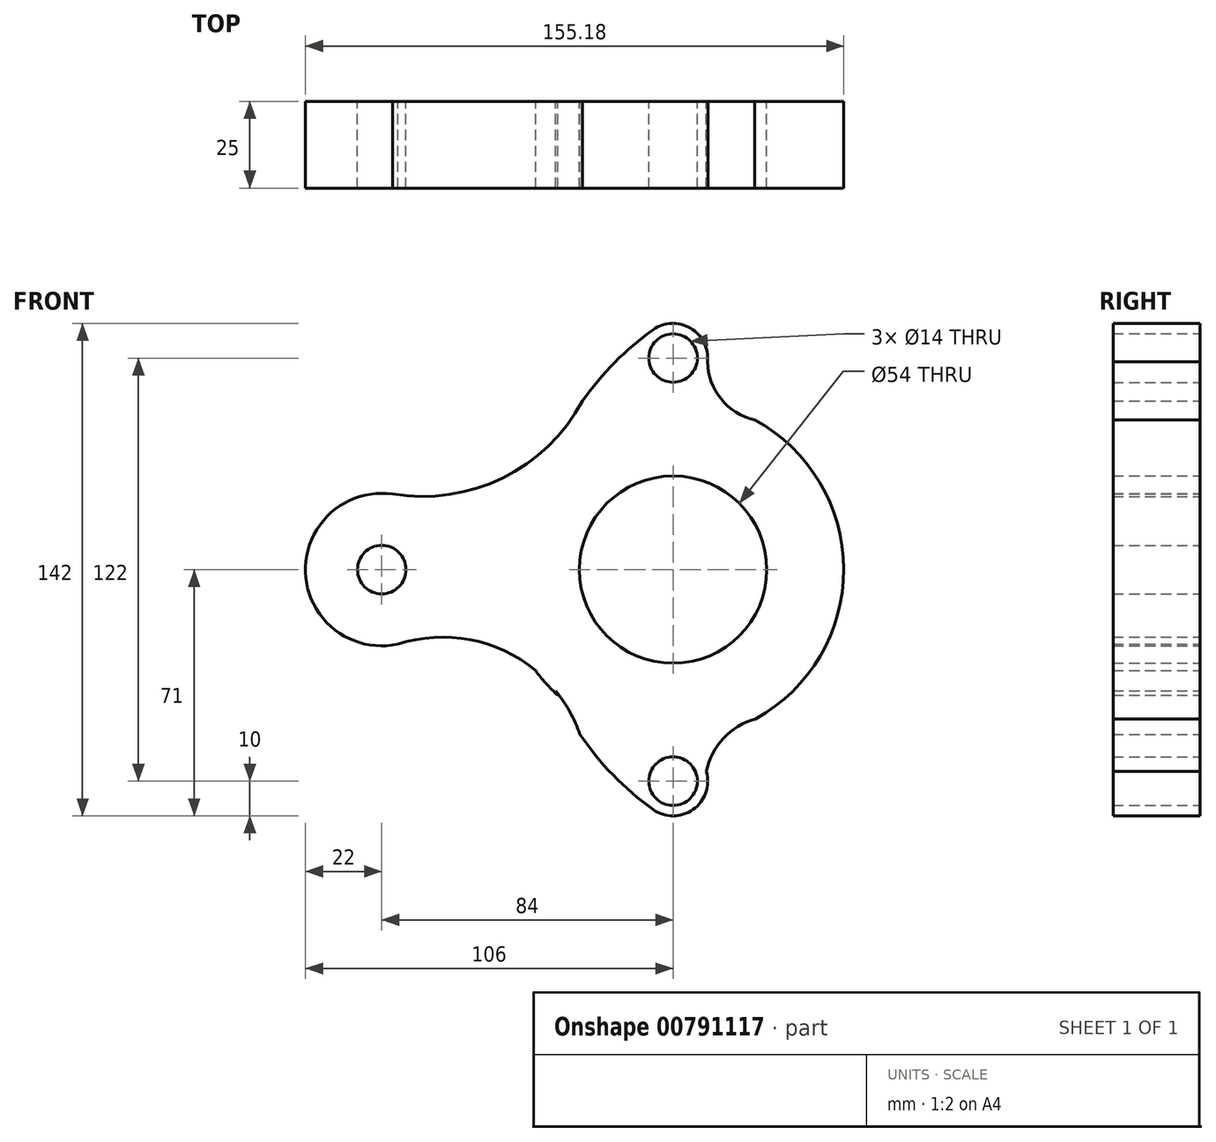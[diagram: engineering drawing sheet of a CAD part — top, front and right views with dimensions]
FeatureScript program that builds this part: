
annotation { "Feature Type Name" : "Feature", "Feature Type Description" : "" }
export const myFeature = defineFeature(function(context is Context, id is Id, definition is map)
    precondition{}
    {
        {
            var Q0;
            Q0=qCreatedBy(makeId("Front.planeOp"),FACE);
            var sketch = newSketch(context, id + "F0", { "sketchPlane" : qUnion([Q0])});
            skArc(sketch, "E0", {"start": v(23.8, -43.04) * mm, "mid": v(49.04, 3.7) * mm, "end": v(17.08, 46.12) * mm});
            skCircle(sketch, "E1", {"center": v(0, 0) * mm, "radius": 27 * mm});
            skLineSegment(sketch, "E2", {"start": v(0, 0) * mm, "end": v(-84, 0) * mm});
            skLineSegment(sketch, "E3", {"start": v(0, 0) * mm, "end": v(0, 61) * mm});
            skLineSegment(sketch, "E4", {"start": v(0, 0) * mm, "end": v(0, -61) * mm});
            skCircle(sketch, "E5", {"center": v(0, 61) * mm, "radius": 7 * mm});
            skCircle(sketch, "E6", {"center": v(0, 61) * mm, "radius": 10 * mm});
            skCircle(sketch, "E7", {"center": v(0, -61) * mm, "radius": 7 * mm});
            skCircle(sketch, "E8", {"center": v(0, -61) * mm, "radius": 10 * mm});
            skCircle(sketch, "E9", {"center": v(-84, 0) * mm, "radius": 7 * mm});
            skArc(sketch, "E10", {"start": v(-80.23, 21.67) * mm, "mid": v(-105.92, -1.9) * mm, "end": v(-76.54, -20.7) * mm});
            skArc(sketch, "E11", {"start": v(-5.82, 69.13) * mm, "mid": v(-16.84, 59.73) * mm, "end": v(-26.1, 48.6) * mm});
            skArc(sketch, "E12", {"start": v(-80.83, 21.77) * mm, "mid": v(-49.17, 26.42) * mm, "end": v(-26.1, 48.6) * mm});
            skArc(sketch, "E13", {"start": v(-26.84, -47.52) * mm, "mid": v(-29.8, -40.95) * mm, "end": v(-33.83, -34.98) * mm});
            skArc(sketch, "E14", {"start": v(23.8, -43.04) * mm, "mid": v(14.53, -48.6) * mm, "end": v(9.6, -58.23) * mm});
            skArc(sketch, "E15", {"start": v(9.94, 59.9) * mm, "mid": v(13.84, 49.2) * mm, "end": v(23.52, 43.2) * mm});
            skArc(sketch, "E16.trimOffspring", {"start": v(-33.83, -34.98) * mm, "mid": v(-33.55, -35.6) * mm, "end": v(-33.26, -36.23) * mm});
            skArc(sketch, "E17.trimOffspring", {"start": v(-39.64, -29.1) * mm, "mid": v(-36.12, -33.38) * mm, "end": v(-32.14, -37.23) * mm});
            skArc(sketch, "E18.trimOffspring", {"start": v(-39.64, -29.1) * mm, "mid": v(-58.52, -20.2) * mm, "end": v(-79.35, -21.5) * mm});
            skArc(sketch, "E19.trimOffspring", {"start": v(-26.84, -47.52) * mm, "mid": v(-17.3, -59.26) * mm, "end": v(-5.82, -69.13) * mm});
            skSolve(sketch);
        }
        {
            var Q0;
            Q0=makeQuery(id+"F0.imprint","IMPRINT",FACE,{"disambiguationData":[TD([[makeQuery(id+"F0.imprint","IMPRINT",EDGE,{"derivedFrom":sQuery(id+"F0.wireOp",EDGE,"E9")}),-1.0]])]});
            var Q1;
            {var subQ13=sQuery(id+"F0.wireOp",EDGE,"E14");Q1=makeQuery(id+"F0.imprint","IMPRINT",FACE,{"disambiguationData":[TD([[makeQuery(id+"F0.imprint","IMPRINT",EDGE,{"derivedFrom":subQ13}),-1.0]])]});}
            var Q2;
            Q2=makeQuery(id+"F0.imprint","IMPRINT",FACE,{"disambiguationData":[TD([[makeQuery(id+"F0.imprint","IMPRINT",EDGE,{"derivedFrom":sQuery(id+"F0.wireOp",EDGE,"E7")}),-1.0]])]});
            var Q3;
            Q3=makeQuery(id+"F0.imprint","IMPRINT",FACE,{"disambiguationData":[TD([[makeQuery(id+"F0.imprint","IMPRINT",EDGE,{"derivedFrom":sQuery(id+"F0.wireOp",EDGE,"E5")}),-1.0]])]});
            extrude(context, id + "F1", {"entities" : qUnion([Q0, Q1, Q2, Q3]), "depth" : 25 * mm, "offsetDistance" : 25 * mm});
        }
    });
